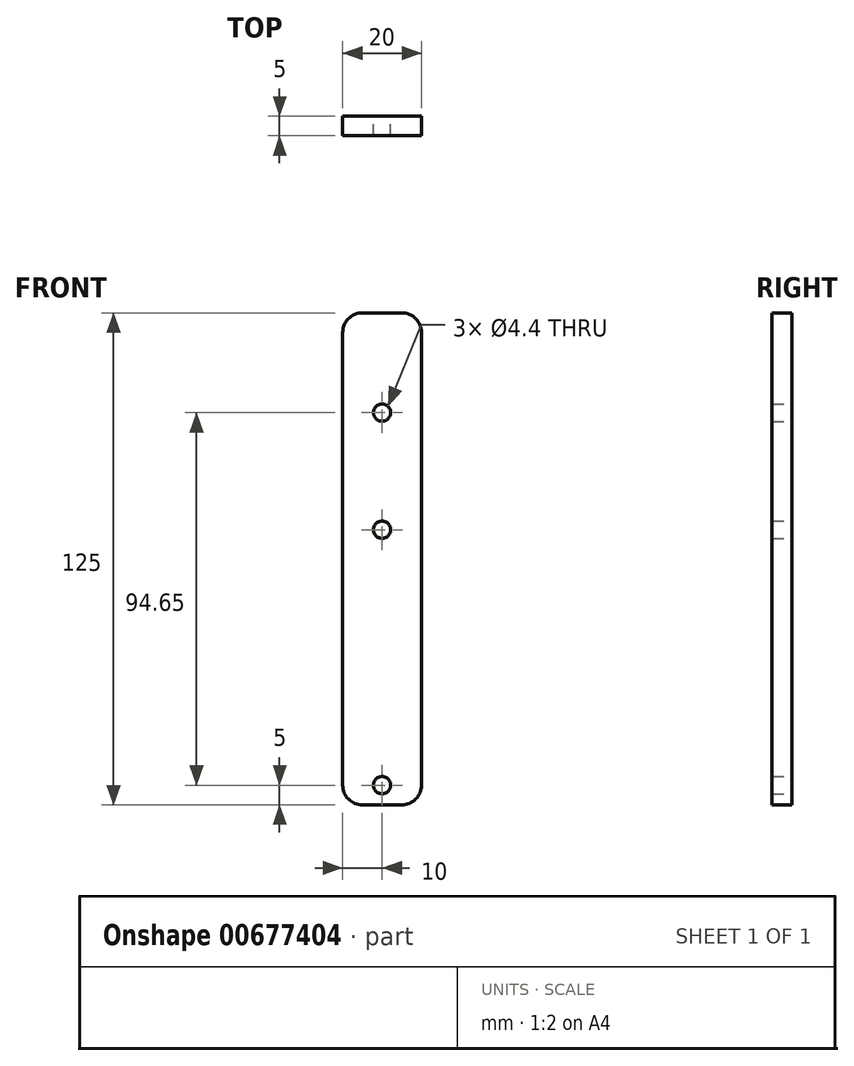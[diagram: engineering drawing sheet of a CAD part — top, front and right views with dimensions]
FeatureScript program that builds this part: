
annotation { "Feature Type Name" : "Feature", "Feature Type Description" : "" }
export const myFeature = defineFeature(function(context is Context, id is Id, definition is map)
    precondition{}
    {
        {
            var Q0;
            Q0=qCreatedBy(makeId("Front.planeOp"),FACE);
            var sketch = newSketch(context, id + "F0", { "sketchPlane" : qUnion([Q0])});
            skLineSegment(sketch, "E0.bottom", {"start": v(10, -62.5) * mm, "end": v(-10, -62.5) * mm});
            skLineSegment(sketch, "E0.top", {"start": v(10, 62.5) * mm, "end": v(-10, 62.5) * mm});
            skLineSegment(sketch, "E0.left", {"start": v(10, -62.5) * mm, "end": v(10, 62.5) * mm});
            skLineSegment(sketch, "E0.right", {"start": v(-10, -62.5) * mm, "end": v(-10, 62.5) * mm});
            skPoint(sketch, "E0.middle", {"position": v(0, 0) * mm});
            skCircle(sketch, "E1", {"center": v(0, -57.5) * mm, "radius": 2.2 * mm});
            skPoint(sketch, "E1.centerSnap0", {"position": v(0, -62.5) * mm});
            skCircle(sketch, "E2", {"center": v(0, 37.15) * mm, "radius": 2.2 * mm});
            skCircle(sketch, "E3", {"center": v(0, 7.4) * mm, "radius": 2.2 * mm});
            skSolve(sketch);
        }
        {
            var Q0;
            Q0 = qSketchRegion(id + "F0", true);
            extrude(context, id + "F1", {"entities" : qUnion([Q0]), "depth" : 5 * mm, "offsetDistance" : 25 * mm});
        }
        {
            var Q0;
            Q0=makeQuery(id+"F1.opExtrude","SWEPT_EDGE",EDGE,{"disambiguationData":[OSD([sQuery(id+"F0.wireOp",EDGE,"E0.top"),sQuery(id+"F0.wireOp",EDGE,"E0.right")])]});
            var Q1;
            Q1=makeQuery(id+"F1.opExtrude","SWEPT_EDGE",EDGE,{"disambiguationData":[OSD([sQuery(id+"F0.wireOp",EDGE,"E0.top"),sQuery(id+"F0.wireOp",EDGE,"E0.left")])]});
            var Q2;
            Q2=makeQuery(id+"F1.opExtrude","SWEPT_EDGE",EDGE,{"disambiguationData":[OSD([sQuery(id+"F0.wireOp",EDGE,"E0.bottom"),sQuery(id+"F0.wireOp",EDGE,"E0.right")])]});
            var Q3;
            Q3=makeQuery(id+"F1.opExtrude","SWEPT_EDGE",EDGE,{"disambiguationData":[OSD([sQuery(id+"F0.wireOp",EDGE,"E0.bottom"),sQuery(id+"F0.wireOp",EDGE,"E0.left")])]});
            fillet(context, id + "F2", {"entities" : qUnion([Q0, Q1, Q2, Q3]), "radius" : 5 * mm, "tangentPropagation" : true, "allowEdgeOverflow" : false});
        }
    });
